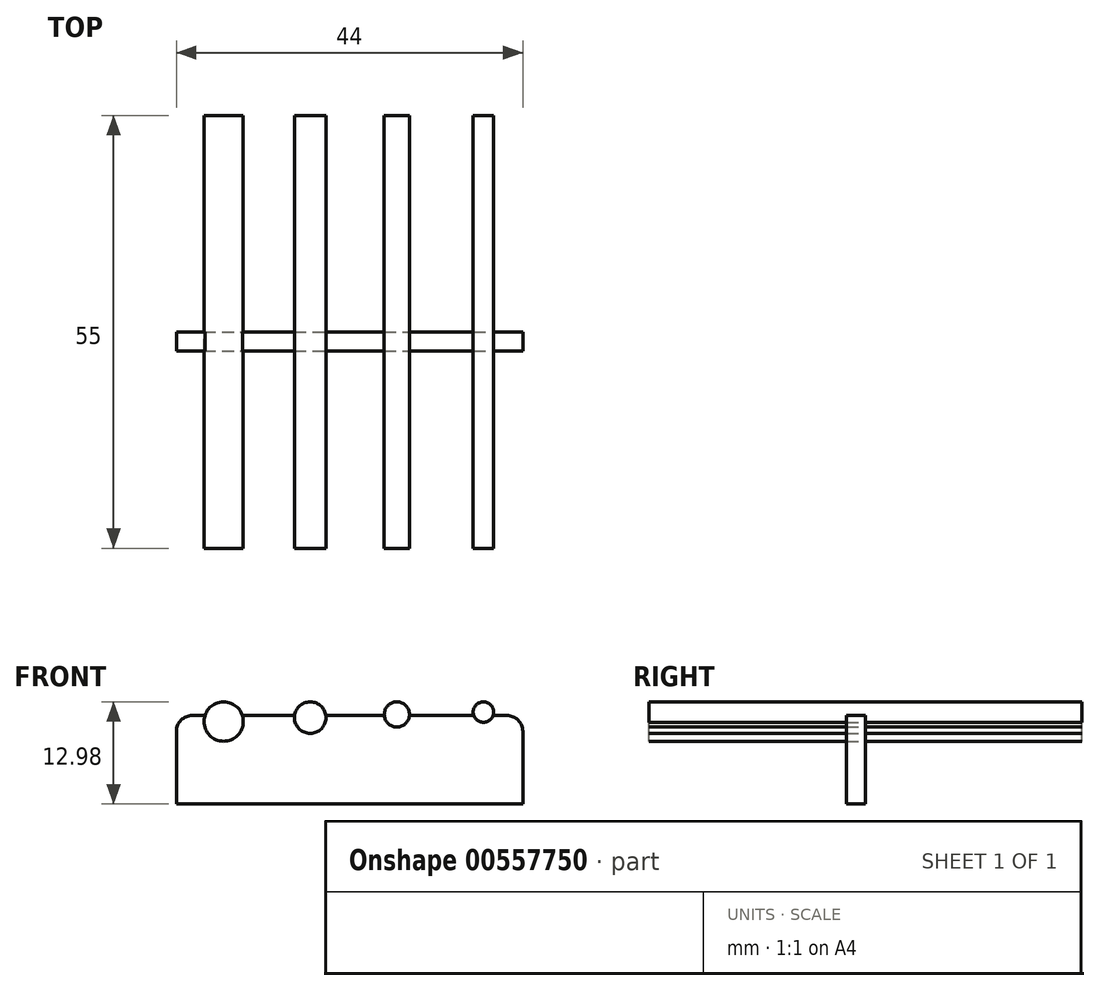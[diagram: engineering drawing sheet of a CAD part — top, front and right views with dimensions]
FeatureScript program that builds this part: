
annotation { "Feature Type Name" : "Feature", "Feature Type Description" : "" }
export const myFeature = defineFeature(function(context is Context, id is Id, definition is map)
    precondition{}
    {
        {
            var Q0;
            Q0=qCreatedBy(makeId("Front.planeOp"),FACE);
            var sketch = newSketch(context, id + "F0", { "sketchPlane" : qUnion([Q0])});
            skCircle(sketch, "E0", {"center": v(-19.92, -2.5) * mm, "radius": 2.5 * mm});
            skCircle(sketch, "E1", {"center": v(-8.92, -2) * mm, "radius": 2 * mm});
            skCircle(sketch, "E2", {"center": v(2.08, -1.6) * mm, "radius": 1.6 * mm});
            skCircle(sketch, "E3", {"center": v(13.08, -1.3) * mm, "radius": 1.3 * mm});
            skLineSegment(sketch, "E4", {"start": v(-19.92, -2.5) * mm, "end": v(-19.92, 0) * mm, "construction": true});
            skLineSegment(sketch, "E5", {"start": v(-8.92, -2) * mm, "end": v(-8.92, 0) * mm, "construction": true});
            skLineSegment(sketch, "E6", {"start": v(2.08, -1.6) * mm, "end": v(2.08, 0) * mm, "construction": true});
            skLineSegment(sketch, "E7", {"start": v(13.08, -1.3) * mm, "end": v(13.08, 0) * mm, "construction": true});
            skLineSegment(sketch, "E8.bottom", {"start": v(-25.92, -1.73) * mm, "end": v(18.08, -1.73) * mm});
            skLineSegment(sketch, "E8.top", {"start": v(-25.92, -12.98) * mm, "end": v(18.08, -12.98) * mm});
            skLineSegment(sketch, "E8.left", {"start": v(-25.92, -1.73) * mm, "end": v(-25.92, -12.98) * mm});
            skLineSegment(sketch, "E8.right", {"start": v(18.08, -1.73) * mm, "end": v(18.08, -12.98) * mm});
            skSolve(sketch);
        }
        {
            var Q0;
            {var subQ0=sQuery(id+"F0.wireOp",EDGE,"E8.bottom");var subQ1=sQuery(id+"F0.wireOp",EDGE,"E0");var subQ2=makeQuery(id+"F0.imprint","INTERSECT",VERTEX,{"disambiguationData":[OD(0.0)],"derivedFrom":[subQ1,subQ0]});Q0=makeQuery(id+"F0.imprint","IMPRINT",FACE,{"disambiguationData":[TD([[makeQuery(id+"F0.imprint","IMPRINT",EDGE,{"disambiguationData":[TD([[subQ2,-1.0]])],"derivedFrom":subQ1}),1.0]])]});}
            var Q1;
            {var subQ0=sQuery(id+"F0.wireOp",EDGE,"E8.bottom");var subQ1=sQuery(id+"F0.wireOp",EDGE,"E1");var subQ2=makeQuery(id+"F0.imprint","INTERSECT",VERTEX,{"disambiguationData":[OD(0.0)],"derivedFrom":[subQ1,subQ0]});Q1=makeQuery(id+"F0.imprint","IMPRINT",FACE,{"disambiguationData":[TD([[makeQuery(id+"F0.imprint","IMPRINT",EDGE,{"disambiguationData":[TD([[subQ2,1.0]])],"derivedFrom":subQ1}),1.0]])]});}
            var Q2;
            {var subQ0=sQuery(id+"F0.wireOp",EDGE,"E8.bottom");var subQ1=sQuery(id+"F0.wireOp",EDGE,"E1");var subQ2=makeQuery(id+"F0.imprint","INTERSECT",VERTEX,{"disambiguationData":[OD(0.0)],"derivedFrom":[subQ1,subQ0]});Q2=makeQuery(id+"F0.imprint","IMPRINT",FACE,{"disambiguationData":[TD([[makeQuery(id+"F0.imprint","IMPRINT",EDGE,{"disambiguationData":[TD([[subQ2,-1.0]])],"derivedFrom":subQ1}),1.0]])]});}
            var Q3;
            {var subQ0=sQuery(id+"F0.wireOp",EDGE,"E8.bottom");var subQ1=sQuery(id+"F0.wireOp",EDGE,"E2");var subQ2=makeQuery(id+"F0.imprint","INTERSECT",VERTEX,{"disambiguationData":[OD(0.0)],"derivedFrom":[subQ1,subQ0]});Q3=makeQuery(id+"F0.imprint","IMPRINT",FACE,{"disambiguationData":[TD([[makeQuery(id+"F0.imprint","IMPRINT",EDGE,{"disambiguationData":[TD([[subQ2,1.0]])],"derivedFrom":subQ1}),1.0]])]});}
            var Q4;
            {var subQ0=sQuery(id+"F0.wireOp",EDGE,"E8.bottom");var subQ1=sQuery(id+"F0.wireOp",EDGE,"E2");var subQ2=makeQuery(id+"F0.imprint","INTERSECT",VERTEX,{"disambiguationData":[OD(0.0)],"derivedFrom":[subQ1,subQ0]});Q4=makeQuery(id+"F0.imprint","IMPRINT",FACE,{"disambiguationData":[TD([[makeQuery(id+"F0.imprint","IMPRINT",EDGE,{"disambiguationData":[TD([[subQ2,-1.0]])],"derivedFrom":subQ1}),1.0]])]});}
            var Q5;
            {var subQ0=sQuery(id+"F0.wireOp",EDGE,"E8.bottom");var subQ1=sQuery(id+"F0.wireOp",EDGE,"E0");var subQ2=makeQuery(id+"F0.imprint","INTERSECT",VERTEX,{"disambiguationData":[OD(0.0)],"derivedFrom":[subQ1,subQ0]});Q5=makeQuery(id+"F0.imprint","IMPRINT",FACE,{"disambiguationData":[TD([[makeQuery(id+"F0.imprint","IMPRINT",EDGE,{"disambiguationData":[TD([[subQ2,1.0]])],"derivedFrom":subQ1}),1.0]])]});}
            var Q6;
            {var subQ0=sQuery(id+"F0.wireOp",EDGE,"E8.bottom");var subQ1=sQuery(id+"F0.wireOp",EDGE,"E3");var subQ2=makeQuery(id+"F0.imprint","INTERSECT",VERTEX,{"disambiguationData":[OD(0.0)],"derivedFrom":[subQ1,subQ0]});Q6=makeQuery(id+"F0.imprint","IMPRINT",FACE,{"disambiguationData":[TD([[makeQuery(id+"F0.imprint","IMPRINT",EDGE,{"disambiguationData":[TD([[subQ2,1.0]])],"derivedFrom":subQ1}),1.0]])]});}
            var Q7;
            {var subQ0=sQuery(id+"F0.wireOp",EDGE,"E8.bottom");var subQ1=sQuery(id+"F0.wireOp",EDGE,"E3");var subQ2=makeQuery(id+"F0.imprint","INTERSECT",VERTEX,{"disambiguationData":[OD(0.0)],"derivedFrom":[subQ1,subQ0]});Q7=makeQuery(id+"F0.imprint","IMPRINT",FACE,{"disambiguationData":[TD([[makeQuery(id+"F0.imprint","IMPRINT",EDGE,{"disambiguationData":[TD([[subQ2,-1.0]])],"derivedFrom":subQ1}),1.0]])]});}
            extrude(context, id + "F1", {"entities" : qUnion([Q0, Q1, Q2, Q3, Q4, Q5, Q6, Q7]), "endBound" : BoundingType.SYMMETRIC, "depth" : 55 * mm, "offsetDistance" : 25 * mm});
        }
        {
            var Q0;
            Q0=makeQuery(id+"F0.imprint","IMPRINT",FACE,{"disambiguationData":[TD([[makeQuery(id+"F0.imprint","IMPRINT",EDGE,{"derivedFrom":sQuery(id+"F0.wireOp",EDGE,"E8.top")}),1.0]])]});
            extrude(context, id + "F2", {"entities" : qUnion([Q0]), "depth" : 2.4 * mm, "offsetDistance" : 25 * mm});
        }
        {
            var Q0;
            Q0=makeQuery(id+"F2.opExtrude","SWEPT_EDGE",EDGE,{"disambiguationData":[OSD([sQuery(id+"F0.wireOp",EDGE,"E8.bottom"),sQuery(id+"F0.wireOp",EDGE,"E8.right")])]});
            var Q1;
            Q1=makeQuery(id+"F2.opExtrude","SWEPT_EDGE",EDGE,{"disambiguationData":[OSD([sQuery(id+"F0.wireOp",EDGE,"E8.bottom"),sQuery(id+"F0.wireOp",EDGE,"E8.left")])]});
            fillet(context, id + "F3", {"entities" : qUnion([Q0, Q1]), "radius" : 2 * mm, "tangentPropagation" : true, "allowEdgeOverflow" : false});
        }
    });
